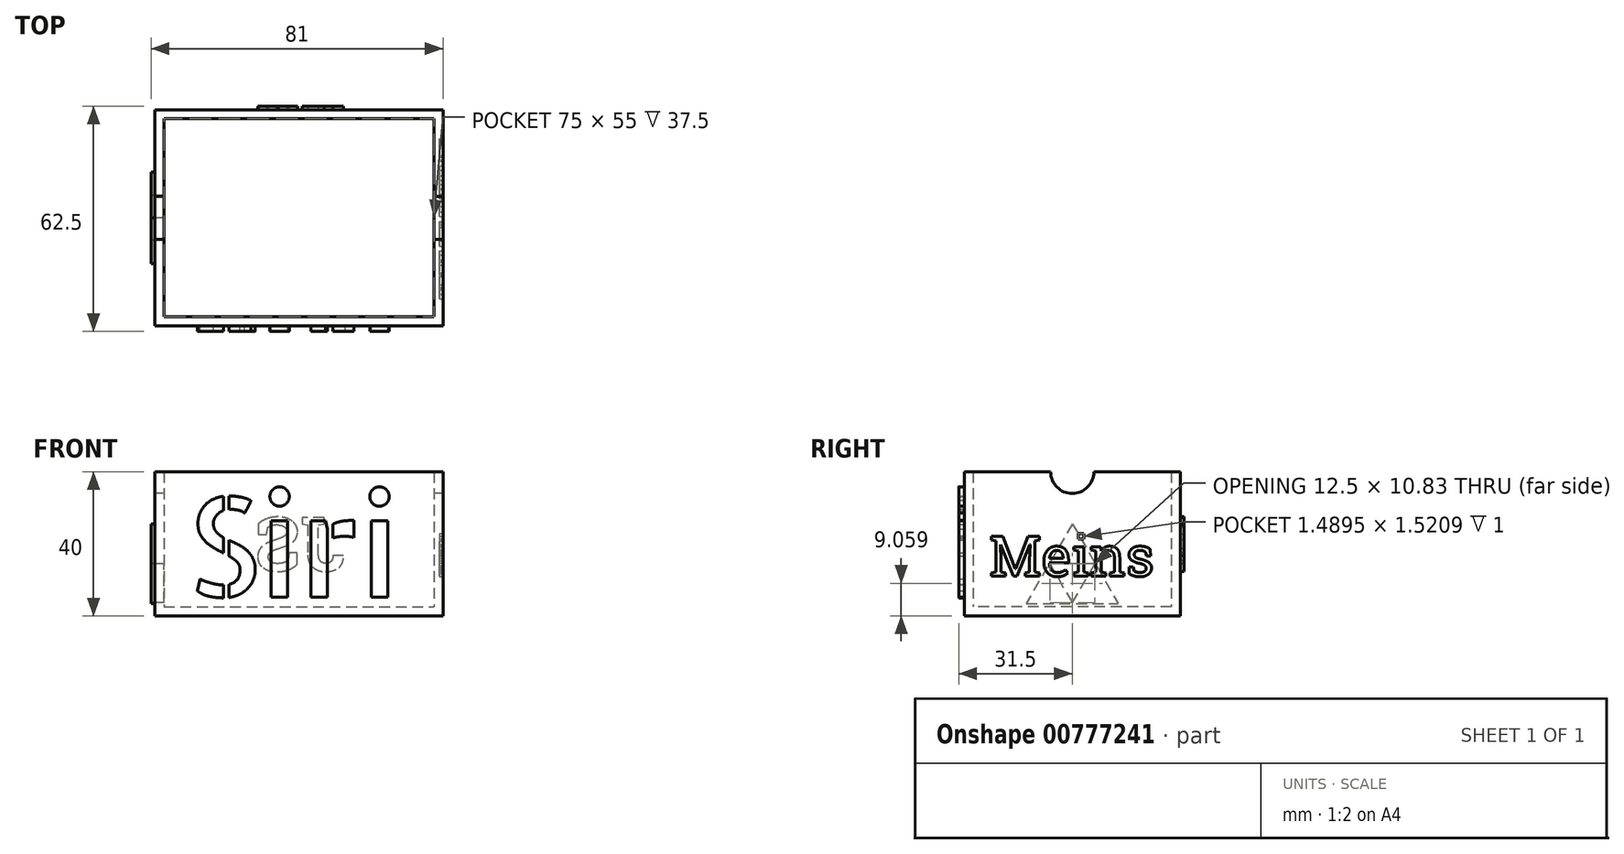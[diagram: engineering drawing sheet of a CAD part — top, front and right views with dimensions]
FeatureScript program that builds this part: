
annotation { "Feature Type Name" : "Feature", "Feature Type Description" : "" }
export const myFeature = defineFeature(function(context is Context, id is Id, definition is map)
    precondition{}
    {
        {
            var Q0;
            Q0=qCreatedBy(makeId("Top.planeOp"),FACE);
            var sketch = newSketch(context, id + "F0", { "sketchPlane" : qUnion([Q0])});
            skLineSegment(sketch, "E0.bottom", {"start": v(-40, 30) * mm, "end": v(40, 30) * mm});
            skLineSegment(sketch, "E0.top", {"start": v(-40, -30) * mm, "end": v(40, -30) * mm});
            skLineSegment(sketch, "E0.left", {"start": v(-40, 30) * mm, "end": v(-40, -30) * mm});
            skLineSegment(sketch, "E0.right", {"start": v(40, 30) * mm, "end": v(40, -30) * mm});
            skSolve(sketch);
        }
        {
            var Q0;
            Q0 = qSketchRegion(id + "F0", true);
            extrude(context, id + "F1", {"entities" : qUnion([Q0]), "depth" : 40 * mm, "offsetDistance" : 25 * mm});
        }
        {
            var Q0;
            Q0=makeQuery(id+"F1.opExtrude","CAP_FACE",FACE,{"disambiguationData":[OSD([sQuery(id+"F0.wireOp",EDGE,"E0.bottom"),sQuery(id+"F0.wireOp",EDGE,"E0.top"),sQuery(id+"F0.wireOp",EDGE,"E0.left"),sQuery(id+"F0.wireOp",EDGE,"E0.right")])],"isStart":false});
            shell(context, id + "F2", {"entities" : qUnion([Q0]), "thickness" : 2.5 * mm});
        }
        {
            var Q0;
            Q0=makeQuery(id+"F1.opExtrude","SWEPT_FACE",FACE,{"disambiguationData":[OSD([sQuery(id+"F0.wireOp",EDGE,"E0.left")])]});
            var sketch = newSketch(context, id + "F3", { "sketchPlane" : qUnion([Q0])});
            skArc(sketch, "E1", {"start": v(-6, 40) * mm, "mid": v(0, 34) * mm, "end": v(6, 40) * mm});
            skSolve(sketch);
        }
        {
            var Q0;
            {var subQ0=sQuery(id+"F3.wireOp",EDGE,"E1");Q0=makeQuery(id+"F3.imprint","IMPRINT",FACE,{"disambiguationData":[TD([[makeQuery(id+"F3.imprint","IMPRINT",EDGE,{"derivedFrom":subQ0}),1.0]])]});}
            extrude(context, id + "F4", {"entities" : qUnion([Q0]), "operationType" : NewBodyOperationType.REMOVE, "oppositeDirection" : true, "depth" : 87.8 * mm, "offsetDistance" : 25 * mm});
        }
        {
            var Q0;
            Q0=makeQuery(id+"F1.opExtrude","SWEPT_FACE",FACE,{"disambiguationData":[OSD([sQuery(id+"F0.wireOp",EDGE,"E0.bottom")])]});
            var sketch = newSketch(context, id + "F5", { "sketchPlane" : qUnion([Q0])});
            skText(sketch, "E2", { "text": "JS", "fontName": "RobotoSlab-Bold.ttf"});
            const initialGuessF5  = {"E2": [-0.01272, 0.0125, 1, 0, 0.015]};
            skSetInitialGuess(sketch, initialGuessF5);
            skSolve(sketch);
        }
        {
            var Q0;
            Q0 = qSketchRegion(id + "F5", true);
            extrude(context, id + "F6", {"entities" : qUnion([Q0]), "operationType" : NewBodyOperationType.ADD, "depth" : 1 * mm, "offsetDistance" : 25 * mm});
        }
        {
            var Q0;
            Q0=makeQuery(id+"F1.opExtrude","SWEPT_FACE",FACE,{"disambiguationData":[OSD([sQuery(id+"F0.wireOp",EDGE,"E0.left")])]});
            var sketch = newSketch(context, id + "F7", { "sketchPlane" : qUnion([Q0])});
            skLineSegment(sketch, "E3", {"start": v(0, 25.57) * mm, "end": v(-12.75, 3.49) * mm});
            skLineSegment(sketch, "E4", {"start": v(12.75, 3.49) * mm, "end": v(-12.75, 3.49) * mm});
            skLineSegment(sketch, "E5", {"start": v(0, 25.57) * mm, "end": v(12.75, 3.49) * mm});
            skLineSegment(sketch, "E6", {"start": v(-6.37, 14.53) * mm, "end": v(6.38, 14.53) * mm});
            skLineSegment(sketch, "E7", {"start": v(6.38, 14.53) * mm, "end": v(0, 3.49) * mm});
            skLineSegment(sketch, "E8", {"start": v(-6.37, 14.53) * mm, "end": v(0, 3.49) * mm});
            skSolve(sketch);
        }
        {
            var Q0;
            {var subQ3=sQuery(id+"F7.wireOp",EDGE,"E6");Q0=makeQuery(id+"F7.imprint","IMPRINT",FACE,{"disambiguationData":[TD([[makeQuery(id+"F7.imprint","IMPRINT",EDGE,{"derivedFrom":subQ3}),1.0]])]});}
            var Q1;
            {var subQ3=sQuery(id+"F7.wireOp",EDGE,"E8");Q1=makeQuery(id+"F7.imprint","IMPRINT",FACE,{"disambiguationData":[TD([[makeQuery(id+"F7.imprint","IMPRINT",EDGE,{"derivedFrom":subQ3}),-1.0]])]});}
            var Q2;
            Q2=makeQuery(id+"F7.imprint","IMPRINT",FACE,{"disambiguationData":[TD([[makeQuery(id+"F7.imprint","IMPRINT",EDGE,{"derivedFrom":sQuery(id+"F7.wireOp",EDGE,"E6")}),-1.0]])]});
            var Q3;
            {var subQ3=sQuery(id+"F7.wireOp",EDGE,"E7");Q3=makeQuery(id+"F7.imprint","IMPRINT",FACE,{"disambiguationData":[TD([[makeQuery(id+"F7.imprint","IMPRINT",EDGE,{"derivedFrom":subQ3}),1.0]])]});}
            extrude(context, id + "F8", {"entities" : qUnion([Q0, Q1, Q2, Q3]), "operationType" : NewBodyOperationType.ADD, "depth" : 1 * mm, "offsetDistance" : 25 * mm});
        }
        {
            var Q0;
            Q0=makeQuery(id+"F8.opExtrude","CAP_FACE",FACE,{"disambiguationData":[OSD([sQuery(id+"F7.wireOp",EDGE,"E3"),sQuery(id+"F7.wireOp",EDGE,"E4"),sQuery(id+"F7.wireOp",EDGE,"E5")])],"isStart":false});
            var sketch = newSketch(context, id + "F9", { "sketchPlane" : qUnion([Q0])});
            skLineSegment(sketch, "E9", {"start": v(-6.25, 14.47) * mm, "end": v(0, 3.65) * mm});
            skLineSegment(sketch, "E10", {"start": v(0, 3.65) * mm, "end": v(6.25, 14.47) * mm});
            skLineSegment(sketch, "E11", {"start": v(6.25, 14.47) * mm, "end": v(-6.25, 14.47) * mm});
            skSolve(sketch);
        }
        {
            var Q0;
            Q0 = qSketchRegion(id + "F9", true);
            extrude(context, id + "F10", {"entities" : qUnion([Q0]), "operationType" : NewBodyOperationType.REMOVE, "oppositeDirection" : true, "depth" : 5 * mm, "offsetDistance" : 25 * mm});
        }
        {
            var Q0;
            Q0=makeQuery(id+"F1.opExtrude","SWEPT_FACE",FACE,{"disambiguationData":[OSD([sQuery(id+"F0.wireOp",EDGE,"E0.top")])]});
            var sketch = newSketch(context, id + "F11", { "sketchPlane" : qUnion([Q0])});
            skText(sketch, "E12", { "text": "Siri", "fontName": "AllertaStencil-Regular.ttf"});
            const initialGuessF11  = {"E12": [-0.03126, 0.00516, 1, 0, 0.02772]};
            skSetInitialGuess(sketch, initialGuessF11);
            skSolve(sketch);
        }
        {
            var Q0;
            Q0 = qSketchRegion(id + "F11", true);
            extrude(context, id + "F12", {"entities" : qUnion([Q0]), "operationType" : NewBodyOperationType.ADD, "depth" : 1.5 * mm, "offsetDistance" : 25 * mm});
        }
        {
            var Q0;
            Q0=makeQuery(id+"F1.opExtrude","SWEPT_FACE",FACE,{"disambiguationData":[OSD([sQuery(id+"F0.wireOp",EDGE,"E0.right")])]});
            var sketch = newSketch(context, id + "F13", { "sketchPlane" : qUnion([Q0])});
            skText(sketch, "E13", { "text": "Meins", "fontName": "RobotoSlab-Regular.ttf"});
            const initialGuessF13  = {"E13": [-0.023, 0.01104, 1, 0, 0.01116]};
            skSetInitialGuess(sketch, initialGuessF13);
            skSolve(sketch);
        }
        {
            var Q0;
            Q0 = qSketchRegion(id + "F13", true);
            extrude(context, id + "F14", {"entities" : qUnion([Q0]), "operationType" : NewBodyOperationType.REMOVE, "oppositeDirection" : true, "depth" : 1 * mm, "offsetDistance" : 25 * mm});
        }
    });
